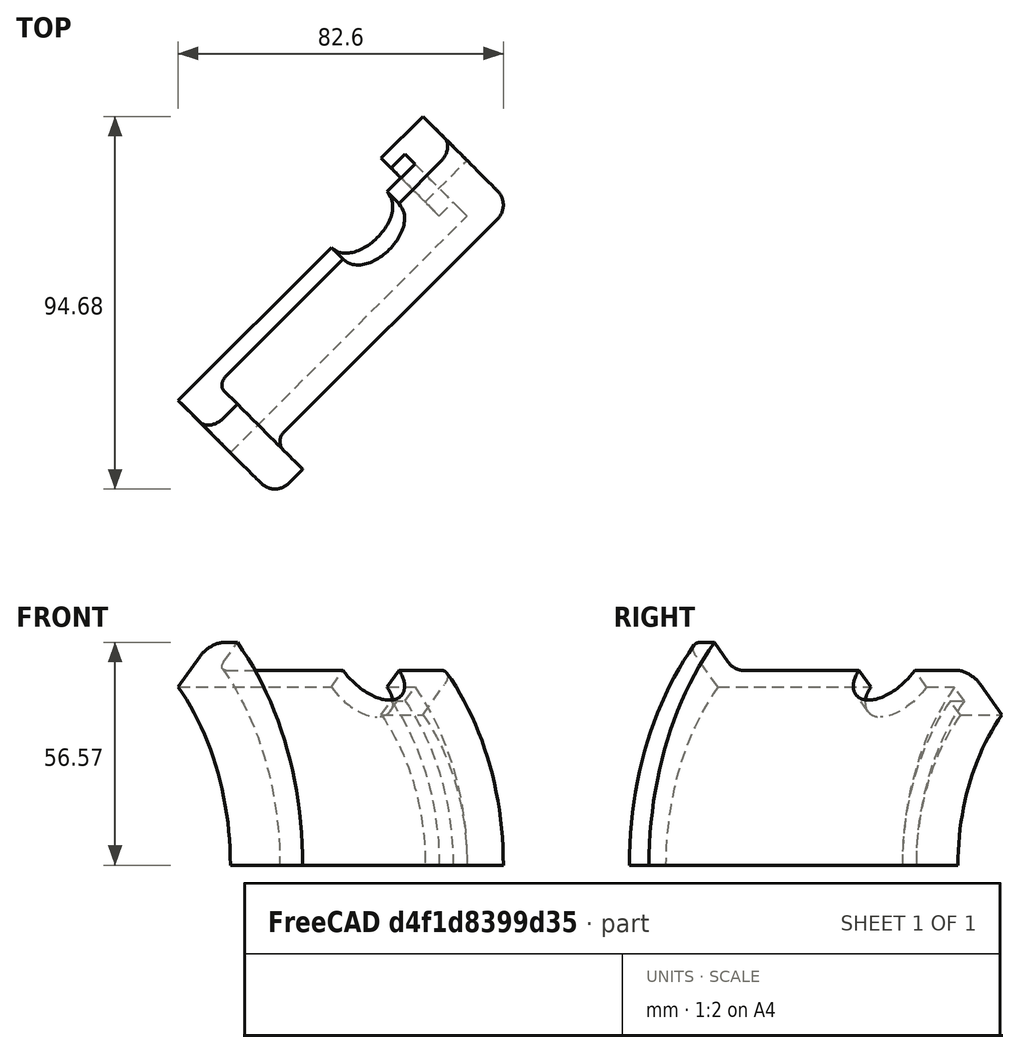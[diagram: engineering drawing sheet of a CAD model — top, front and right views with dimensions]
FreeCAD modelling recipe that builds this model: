
FCSTD DOCUMENT  (FreeCAD 0.15R4671 (Git))
Label: sphere_support_cyls4_w6
License: All rights reserved
LicenseURL: http://en.wikipedia.org/wiki/All_rights_reserved
objects: Part::Cut×11, Part::Box×8, Part::Cylinder×6, Part::Fillet×3, Part::MultiFuse×2
note: 30 computed .brp shape members not serialized (recipe doc carries the construction recipe); baked Part::Feature solids carry a one-line shape summary decoded from their .brp

FEATURE [Part::Cylinder] Cylinder  label="Base_Cylinder"
  Angle = 360
  Height = 10
  Radius = 80
FEATURE [Part::Cylinder] Cylinder001  label="Body_Cylinder"
  Angle = 360
  Height = 90
  Placement = pos=(0,0,5) rot=(0,0,1;0rad)
  Radius = 70
FEATURE [Part::MultiFuse] Fusion  label="Core_Fusion"
  Shapes = -> [Cylinder,Cylinder001]
FEATURE [Part::Cylinder] Cylinder002  label="Inner_Hole"
  Angle = 360
  Height = 85
  Radius = 64
FEATURE [Part::Cut] Cut
  Base = -> Fusion
  Tool = -> Cylinder002
FEATURE [Part::Cylinder] Cylinder003  label="Inner_Lip"
  Angle = 360
  Height = 10
  Placement = pos=(0,0,80) rot=(0,0,1;0rad)
  Radius = 59
FEATURE [Part::MultiFuse] Fusion001
  Shapes = -> [Cut,Cylinder003]
FEATURE [Part::Cylinder] Cylinder004  label="Through_Hole"
  Angle = 360
  Height = 100
  Radius = 54
FEATURE [Part::Cut] Cut001
  Base = -> Fusion001
  Tool = -> Cylinder004
FEATURE [Part::Fillet] Fillet
  Base = -> Cut001
  Edges = 1 edges r=3: [Edge12]
FEATURE [Part::Fillet] Fillet001
  Base = -> Fillet
  Edges = 1 edges r=5: [Edge11]
FEATURE [Part::Fillet] Fillet002
  Base = -> Fillet001
  Edges = 1 edges r=5: [Edge13]
FEATURE [Part::Cylinder] Cylinder005  label="Bearing_Holes"
  Angle = 360
  Height = 180
  Placement = pos=(0,90,65) rot=(1,0,0;1.5708rad)
  Radius = 10
FEATURE [Part::Cut] Cut002
  Base = -> Fillet002
  Tool = -> Cylinder005
FEATURE [Part::Box] Box  label="Bearing_Slot"
  Height = 35
  Length = 20
  Placement = pos=(-10,48,65) rot=(0,0,1;0rad)
  Width = 25
FEATURE [Part::Cut] Cut003
  Base = -> Cut002
  Tool = -> Box
FEATURE [Part::Box] Box001  label="Cube"
  Height = 35
  Length = 10
  Placement = pos=(0,48,65) rot=(0,1,0;0.261799rad)
  Width = 25
FEATURE [Part::Cut] Cut004
  Base = -> Cut003
  Tool = -> Box001
FEATURE [Part::Box] Box002  label="Cube001"
  Height = 35
  Length = 10
  Placement = pos=(-9.95,48,64) rot=(0,-1,0;0.261799rad)
  Width = 25
FEATURE [Part::Cut] Cut005
  Base = -> Cut004
  Tool = -> Box002
FEATURE [Part::Box] Box003  label="Tab_Cut_R"
  Height = 80
  Length = 20
  Placement = pos=(63,-10,20) rot=(0,0,1;0rad)
  Width = 20
FEATURE [Part::Cut] Cut006
  Base = -> Cut005
  Tool = -> Box003
FEATURE [Part::Box] Box004  label="Tab_Cut_L"
  Height = 80
  Length = 20
  Placement = pos=(-83,-10,20) rot=(0,0,1;0rad)
  Width = 20
FEATURE [Part::Cut] Cut007
  Base = -> Cut006
  Tool = -> Box004
FEATURE [Part::Box] Box005  label="Cube002"
  Height = 100
  Length = 100
  Placement = pos=(0,0,0) rot=(0,0,1;3.14159rad)
  Width = 100
FEATURE [Part::Cut] Cut008
  Base = -> Cut007
  Tool = -> Box005
FEATURE [Part::Box] Box006  label="Cube003"
  Height = 100
  Length = 100
  Placement = pos=(71,-71,0) rot=(0,0,1;0.785398rad)
  Width = 200
FEATURE [Part::Cut] Cut009
  Base = -> Cut008
  Placement = pos=(0,0,0) rot=(-0.707107,0.707107,0;1.5708rad)
  Tool = -> Box006
FEATURE [Part::Box] Box007  label="Cube004"
  Height = 100
  Length = 100
  Placement = pos=(0,0,0) rot=(0,0,1;0.785398rad)
  Width = 100
FEATURE [Part::Cut] Cut010
  Base = -> Cut009
  Tool = -> Box007
